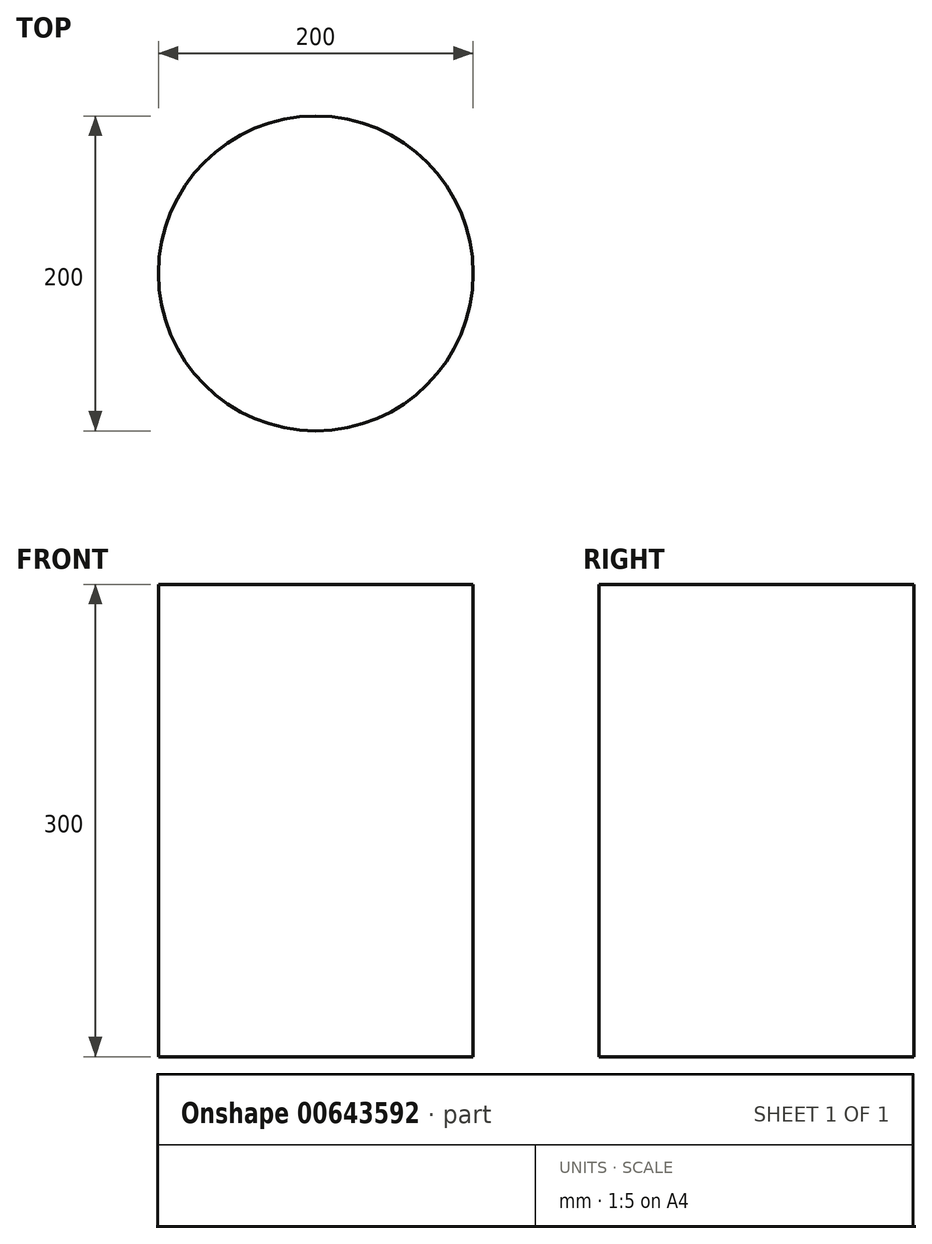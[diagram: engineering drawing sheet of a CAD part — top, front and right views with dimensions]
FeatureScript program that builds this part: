
annotation { "Feature Type Name" : "Feature", "Feature Type Description" : "" }
export const myFeature = defineFeature(function(context is Context, id is Id, definition is map)
    precondition{}
    {
        {
            var Q0;
            Q0=qCreatedBy(makeId("Top.planeOp"),FACE);
            var sketch = newSketch(context, id + "F0", { "sketchPlane" : qUnion([Q0])});
            skCircle(sketch, "E0", {"center": v(0, 0) * mm, "radius": 100 * mm});
            skSolve(sketch);
        }
        {
            var Q0;
            Q0 = qSketchRegion(id + "F0", true);
            extrude(context, id + "F1", {"entities" : qUnion([Q0]), "depth" : 300 * mm, "offsetDistance" : 25 * mm});
        }
    });
